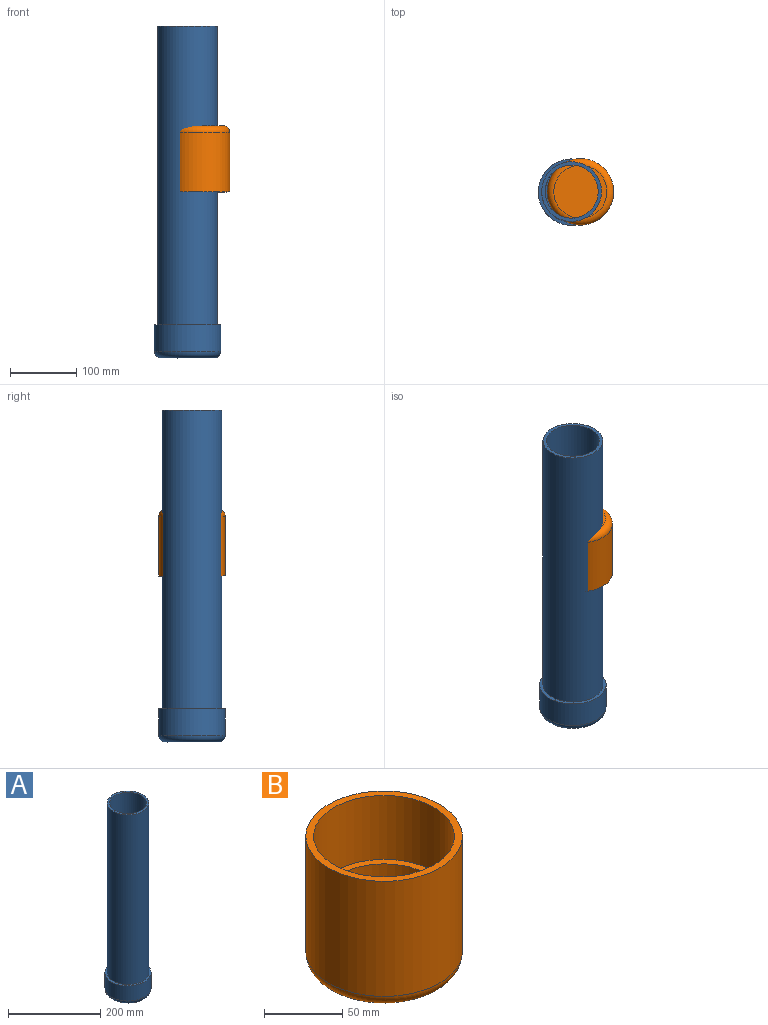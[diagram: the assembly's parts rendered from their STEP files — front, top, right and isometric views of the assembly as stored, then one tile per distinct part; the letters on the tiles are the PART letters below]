
ASSEMBLY  parts=2 mates=1
PART A: 8 faces, bbox 108.2x108.2x500 mm
  f0: cylinder r=40mm len=495mm, axis (0,0,-1), area 124407.1mm2, adj f2,f6
  f1: cylinder r=45mm len=450mm, axis (0,0,-1), area 127234.5mm2, adj f2,f5
  f2: plane 90x90mm, normal (0,0,1), area 1335.2mm2, adj f0,f1
  f3: plane 80x80mm, normal (0,0,-1), area 5026.5mm2, adj f7
  f4: cylinder r=50mm len=100mm, axis (0,0,-1), area 12566.4mm2, adj f5,f7
  f5: plane 100x100mm, normal (0,0,1), area 1492.3mm2, adj f1,f4
  f6: plane 80x80mm, normal (0,0,1), area 5026.5mm2, adj f0
  f7: torus R=40mm, axis (0,0,1), area 4576.2mm2, adj f3,f4
PART B: 8 faces, bbox 108.2x108.2x100 mm
  f0: cylinder r=40mm len=80mm, axis (0,0,-1), area 11309.7mm2, adj f1,f6
  f1: plane 90x90mm, normal (0,0,1), area 1335.2mm2, adj f0,f3
  f2: plane 80x80mm, normal (0,0,-1), area 5026.5mm2, adj f7
  f3: cylinder r=45mm len=90mm, axis (0,0,-1), area 14137.2mm2, adj f1,f5
  f4: cylinder r=50mm len=100mm, axis (0,0,-1), area 28274.3mm2, adj f5,f7
  f5: plane 100x100mm, normal (0,0,1), area 1492.3mm2, adj f3,f4
  f6: plane 80x80mm, normal (0,0,1), area 5026.5mm2, adj f0
  f7: torus R=40mm, axis (0,0,1), area 4576.2mm2, adj f2,f4
PLACE A rot(axis=(0,0,1),0deg) t=(40.14,-33.06,-63.11)mm
PLACE B rot(axis=(0,1,0),180deg) t=(53.45,-33.06,286.89)mm
MATE pin_slot B.f0 <-> A.f0  axis (0,0,1) through (53.45,-33.06,211.89)mm
